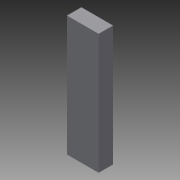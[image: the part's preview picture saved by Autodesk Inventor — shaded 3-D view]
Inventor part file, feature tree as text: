
AUTODESK INVENTOR PART (.ipt)
format: ipt  version: 2014 (Build 180170000, 170)  size: 67,072 bytes
history: native  units: mm
features: extrude x1, sketch x1
ambient origin geometry x8: Origin, YZ Plane, XZ Plane, XY Plane, X Axis, Y Axis, Z Axis, Center Point
bodies: Volumenkörper1 (feature_tree)
feature tree (2):
  extrude  "Extrusion1"  Depth=20.9mm
  sketch  "Skizze1"  dims[d0=5.5mm d1=20.9mm d2=2.5mm d3=0.0mm]
